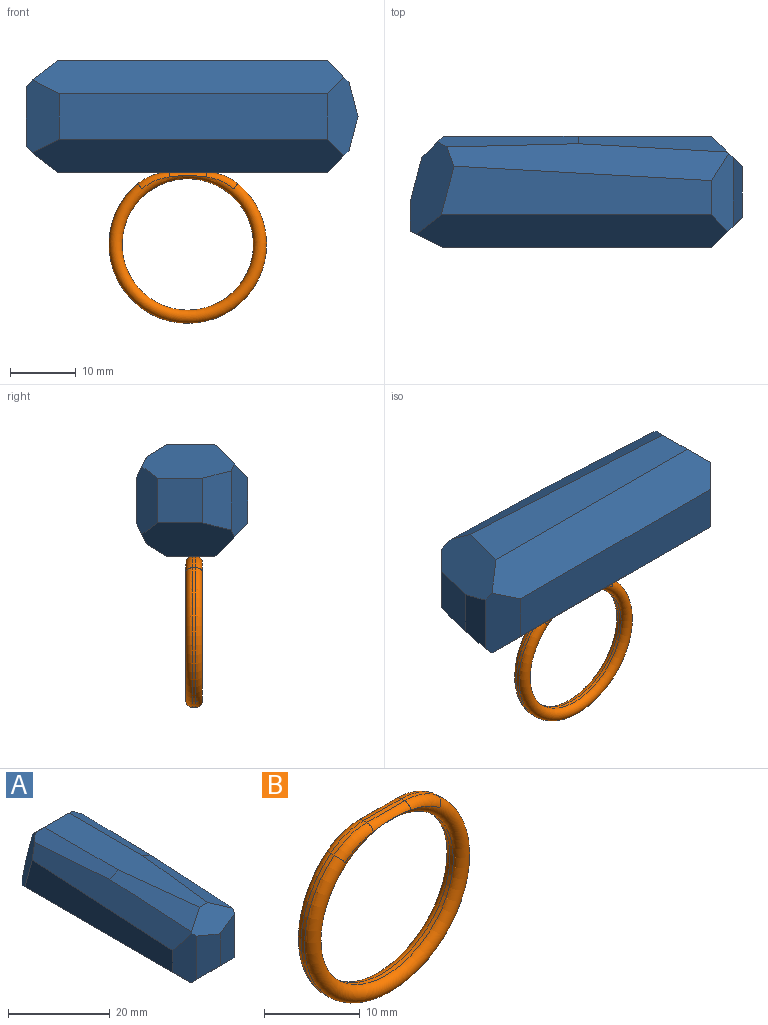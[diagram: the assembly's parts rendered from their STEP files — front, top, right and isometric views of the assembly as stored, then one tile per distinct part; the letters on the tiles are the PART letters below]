
ASSEMBLY  parts=2 mates=1
PART A: 27 faces, bbox 17x50.6x17 mm
  f0: plane 40.84x7mm, normal (0,0,-1), area 285.9mm2, adj f8,f13,f14,f17
  f1: plane 41.15x7.42mm, normal (1,0,0), area 255.1mm2, adj f6,f12,f13,f15
  f2: plane 40.84x6.84mm, normal (0,0,1), area 233.2mm2, adj f4,f5,f7,f9,f21,f22
  f3: plane 9.01x4.3mm, normal (0,1,0), area 34.1mm2, adj f10,f14,f15,f16
  f4: plane 21.38x3.31mm, normal (0.45,0,0.89), area 65.9mm2, adj f2,f5,f7,f12,f15
  f5: plane 22.75x4.59mm, normal (0.45,-0.05,0.89), area 84.7mm2, adj f2,f4,f9,f12
  f6: plane 11.86x3.28mm, normal (0.71,-0.71,0), area 42.2mm2, adj f1,f8,f9,f11,f12,f13
  f7: plane 10.3x3.28mm, normal (0,0.71,0.71), area 39.8mm2, adj f2,f4,f10,f15,f16,f22
  f8: plane 12x4.65mm, normal (0,-0.71,-0.71), area 56.1mm2, adj f0,f6,f11,f13,f17,f19,f20
  f9: plane 11.72x4.65mm, normal (0,-0.71,0.71), area 47.2mm2, adj f2,f5,f6,f11,f12,f18,f19,f20
  f10: plane 6.88x6.84mm, normal (0,0.97,0.25), area 48.6mm2, adj f3,f7,f15,f16
  f11: plane 10.43x5.22mm, normal (0.25,-0.97,0), area 48.9mm2, adj f6,f8,f9,f19
  f12: plane 42.92x5.62mm, normal (0.85,-0.03,0.53), area 198.7mm2, adj f1,f4,f5,f6,f9,f15
  f13: plane 47.46x5mm, normal (0.71,0,-0.71), area 312.8mm2, adj f0,f1,f6,f8,f14,f15
  f14: plane 11.12x5.08mm, normal (0,0.45,-0.89), area 52.5mm2, adj f0,f3,f13,f15,f16,f17
  f15: plane 14.08x6.71mm, normal (0.71,0.68,0.18), area 83.8mm2, adj f1,f3,f4,f7,f10,f12,f13,f14
  f16: plane 14.08x6.71mm, normal (-0.71,0.68,0.18), area 83.8mm2, adj f3,f7,f10,f14,f17,f18,f22,f23
  f17: plane 47.46x5mm, normal (-0.71,0,-0.71), area 312.8mm2, adj f0,f8,f14,f16,f20,f23
  f18: plane 42.92x5.62mm, normal (-0.85,-0.03,0.53), area 198.7mm2, adj f9,f16,f20,f21,f22,f23
  f19: plane 10.43x5.22mm, normal (-0.25,-0.97,0), area 48.9mm2, adj f8,f9,f11,f20
  f20: plane 11.86x3.28mm, normal (-0.71,-0.71,0), area 42.2mm2, adj f8,f9,f17,f18,f19,f23
  f21: plane 22.75x4.59mm, normal (-0.45,-0.05,0.89), area 84.7mm2, adj f2,f9,f18,f22
  f22: plane 21.38x3.31mm, normal (-0.45,0,0.89), area 65.9mm2, adj f2,f7,f16,f18,f21
  f23: plane 41.15x7.42mm, normal (-1,0,0), area 255.1mm2, adj f16,f17,f18,f20
  f24: plane 15x15mm, normal (0,1,0), area 176.7mm2, adj f26
  f25: plane 15x15mm, normal (0,-1,0), area 176.7mm2, adj f26
  f26: cylinder r=7.5mm len=40mm, axis (0,1,0), area 1885mm2, adj f24,f25
PART B: 13 faces, bbox 26x2.5x26 mm
  f0: plane 5.57x0.5mm, normal (0,0,1), area 2.8mm2, adj f3,f4,f8,f12
  f1: cylinder r=10mm len=20mm, axis (0,1,0), area 31.4mm2, adj f5,f9
  f2: cylinder r=12mm len=24mm, axis (0,1,0), area 29.4mm2, adj f3,f4,f5,f9
  f3: cylinder r=7.62mm len=4.85mm, axis (0,1,0), area 2.6mm2, adj f0,f2,f7,f10
  f4: cylinder r=7.62mm len=4.85mm, axis (0,1,0), area 2.6mm2, adj f0,f2,f6,f11
  f5: torus R=11mm, axis (0,-1,0), area 187.9mm2, adj f1,f2,f6,f7,f8
  f6: torus R=6.62mm, axis (0,-1,0), area 7.1mm2, adj f4,f5,f8
  f7: torus R=6.62mm, axis (0,-1,0), area 7.1mm2, adj f3,f5,f8
  f8: cylinder r=1mm len=5.57mm, axis (1,0,0), area 6.2mm2, adj f0,f5,f6,f7
  f9: torus R=11mm, axis (0,-1,0), area 187.9mm2, adj f1,f2,f10,f11,f12
  f10: torus R=6.62mm, axis (0,-1,0), area 7.1mm2, adj f3,f9,f12
  f11: torus R=6.62mm, axis (0,-1,0), area 7.1mm2, adj f4,f9,f12
  f12: cylinder r=1mm len=5.57mm, axis (-1,0,0), area 6.2mm2, adj f0,f9,f10,f11
PLACE A rot(axis=(-0.58,0.58,0.58),120deg) t=(50.44,27.95,21.03)mm
PLACE B t=(49.08,28.87,1.53)mm
MATE fastened A.f1 <-> B.f0  axis (0,0,-1) through (49.08,27.62,12.53)mm
